# Revit family: CEMCO-ProXHeaderOuter
name_source: partatom
category: Structural Framing
units: mm (PartAtom-declared; Revit-internal decimal feet)

## family parameters
Always export as geometry = No
Always vertical = Yes
Classification Number = 23.25.30.11.14.14
Cut with Voids When Loaded = No
Material for Model Behavior = Other
Section Shape = Not Defined
Shared = No
Show family pre-cut in plan views = Yes

## types (3) — shared parameters
BIMSF_Filter = ProX Header, MWF
Description = CEMCO ProX Header®
Height = 4.25 "
Height1 = 4.215 "
Height2 = 1.391 "
Keynote = 092216
Manufacturer = CEMCO
Model = V1
Product Info = ProX Header®
Product Submittal Link = https://cemcosteel.com
Thickness = 0.035 "
URL = https://cemcosteel.com
Width = 8 "
Width1 = 7.93 "
Width2 = 1.898 "
Width3 = 0.988 "
Width4 = 1.828 "
Width5 = 0.918 "
bf = 4.25 "
d = 8 "
tf = 0.035 "
zero-valued in all types: Xcg

## per-type parameters (varying)
| type | Assembly Code |
| 362X425-33 | B1010 |
| 400X425-33 | B1010 |
| 600X425-33 | C1010100 |

## geometry (parser evidence)
native form markers: Sweep x2
no freeform markers — native parametric forms only
